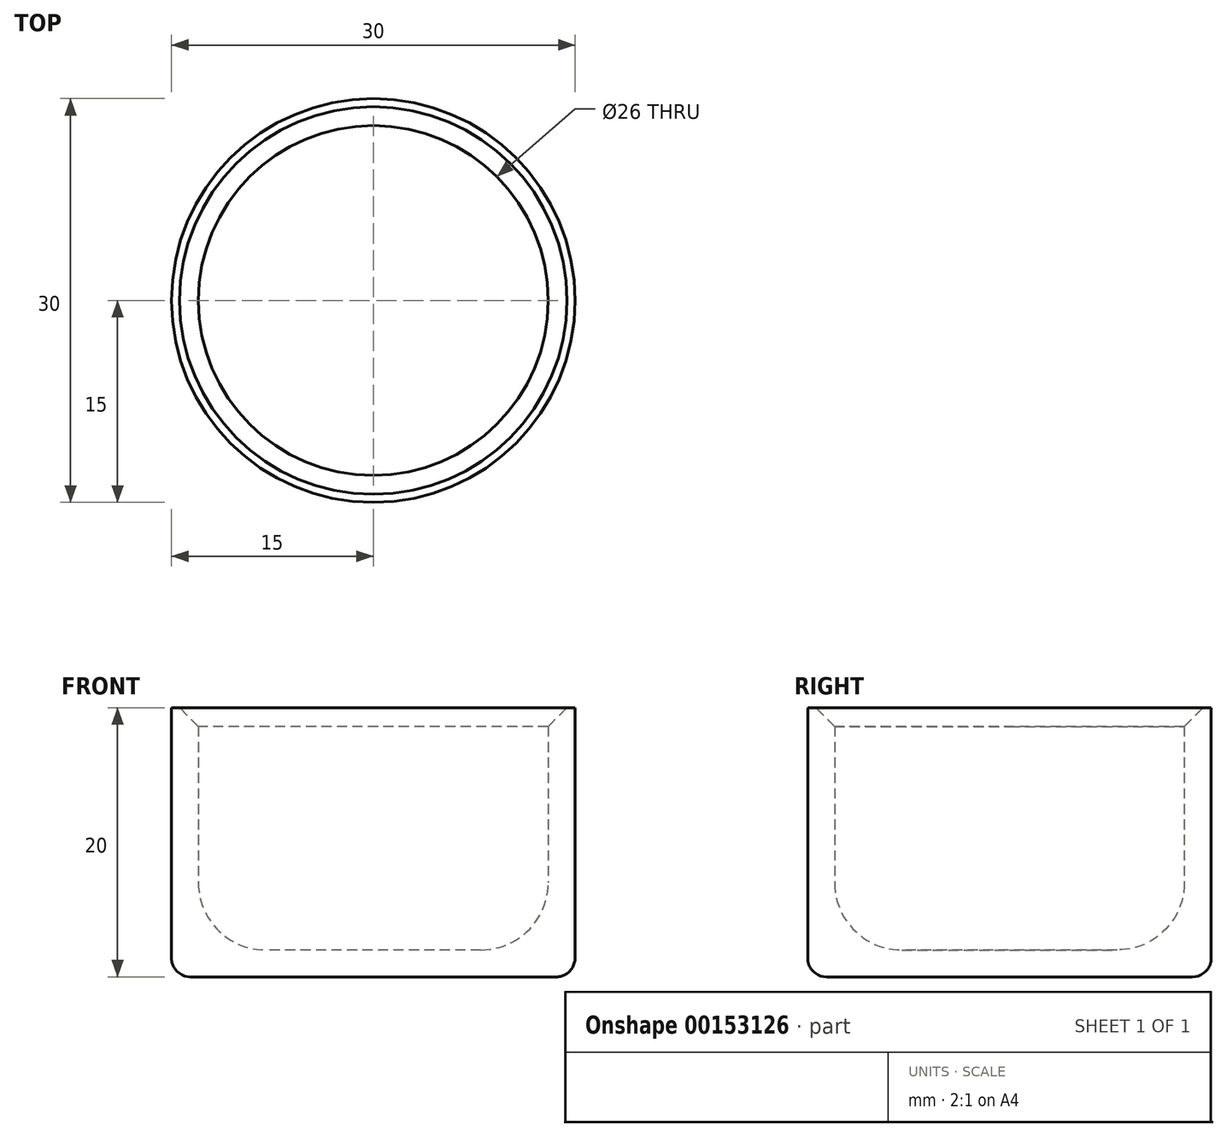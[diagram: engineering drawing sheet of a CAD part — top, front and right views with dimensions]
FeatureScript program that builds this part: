
annotation { "Feature Type Name" : "Feature", "Feature Type Description" : "" }
export const myFeature = defineFeature(function(context is Context, id is Id, definition is map)
    precondition{}
    {
        {
            var Q0;
            Q0=qCreatedBy(makeId("Top.planeOp"),FACE);
            var sketch = newSketch(context, id + "F0", { "sketchPlane" : qUnion([Q0])});
            skCircle(sketch, "E0", {"center": v(0, 0) * mm, "radius": 15 * mm});
            skCircle(sketch, "E1", {"center": v(0, 0) * mm, "radius": 13 * mm});
            skSolve(sketch);
        }
        {
            var Q0;
            Q0=makeQuery(id+"F0.imprint","IMPRINT",FACE,{"disambiguationData":[TD([[makeQuery(id+"F0.imprint","IMPRINT",EDGE,{"derivedFrom":sQuery(id+"F0.wireOp",EDGE,"E1")}),1.0]])]});
            var Q1;
            Q1=makeQuery(id+"F0.imprint","IMPRINT",FACE,{"disambiguationData":[TD([[makeQuery(id+"F0.imprint","IMPRINT",EDGE,{"derivedFrom":sQuery(id+"F0.wireOp",EDGE,"E0")}),1.0]])]});
            extrude(context, id + "F1", {"entities" : qUnion([Q0, Q1]), "depth" : 2 * mm});
        }
        {
            var Q0;
            Q0=makeQuery(id+"F0.imprint","IMPRINT",FACE,{"disambiguationData":[TD([[makeQuery(id+"F0.imprint","IMPRINT",EDGE,{"derivedFrom":sQuery(id+"F0.wireOp",EDGE,"E0")}),1.0]])]});
            extrude(context, id + "F2", {"entities" : qUnion([Q0]), "operationType" : NewBodyOperationType.ADD, "depth" : 20 * mm});
        }
        {
            var Q0;
            Q0=makeQuery(id+"F2.boolean.opBoolean","INTERSECT",EDGE,{"derivedFrom":[makeQuery(id+"F1.opExtrude","CAP_FACE",FACE,{"disambiguationData":[OSD([sQuery(id+"F0.wireOp",EDGE,"E0")])],"isStart":false}),makeQuery(id+"F2.opExtrude","SWEPT_FACE",FACE,{"disambiguationData":[OSD([sQuery(id+"F0.wireOp",EDGE,"E1")])]})]});
            fillet(context, id + "F3", {"entities" : qUnion([Q0]), "radius" : 5 * mm, "tangentPropagation" : true, "allowEdgeOverflow" : false});
        }
        {
            var Q0;
            Q0=makeQuery(id+"F2.opExtrude","CAP_EDGE",EDGE,{"disambiguationData":[OSD([sQuery(id+"F0.wireOp",EDGE,"E1")])],"isStart":false});
            chamfer(context, id + "F4", {"entities" : qUnion([Q0]), "width" : 1.4 * mm, "tangentPropagation" : true});
        }
        {
            var Q0;
            Q0=makeQuery(id+"F1.opExtrude","CAP_EDGE",EDGE,{"disambiguationData":[OSD([sQuery(id+"F0.wireOp",EDGE,"E0")])],"isStart":true});
            fillet(context, id + "F5", {"entities" : qUnion([Q0]), "radius" : 1.4 * mm, "tangentPropagation" : true, "allowEdgeOverflow" : false});
        }
    });
